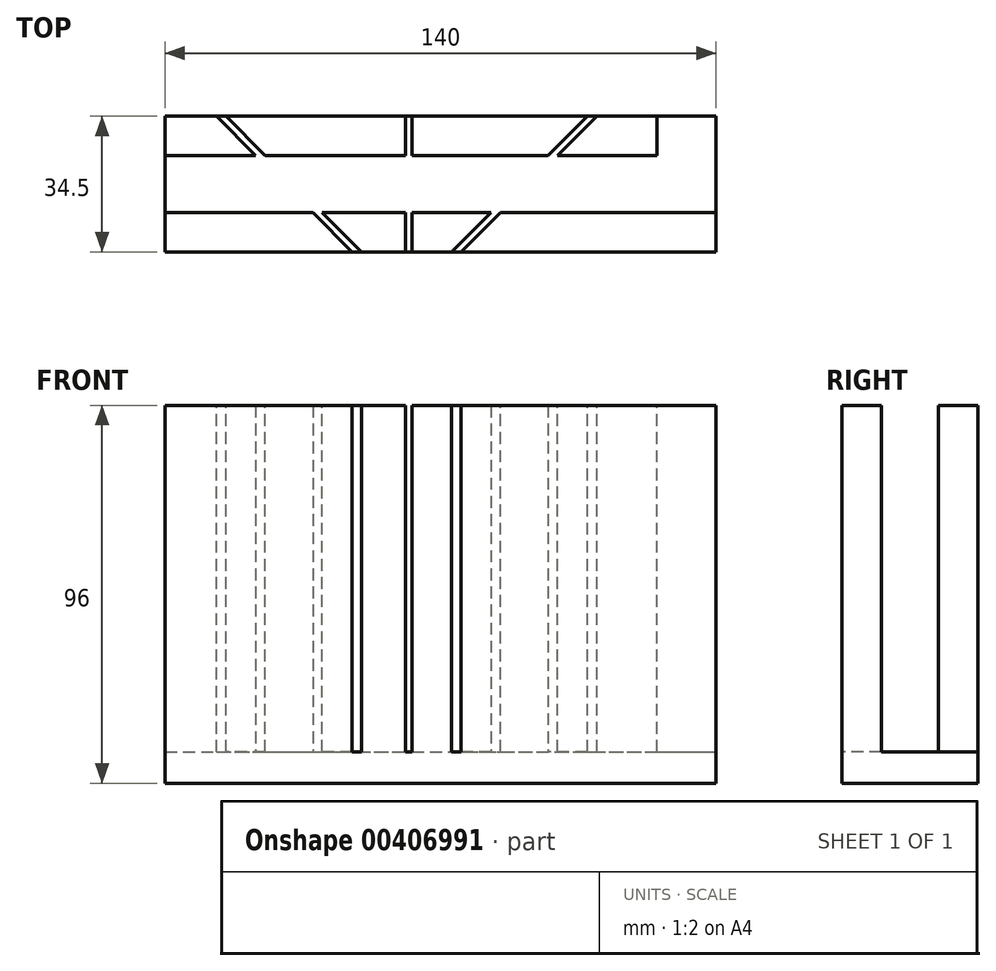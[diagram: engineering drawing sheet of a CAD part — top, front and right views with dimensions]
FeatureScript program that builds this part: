
annotation { "Feature Type Name" : "Feature", "Feature Type Description" : "" }
export const myFeature = defineFeature(function(context is Context, id is Id, definition is map)
    precondition{}
    {
        {
            var Q0;
            Q0=qCreatedBy(makeId("Top.planeOp"),FACE);
            var sketch = newSketch(context, id + "F0", { "sketchPlane" : qUnion([Q0])});
            skLineSegment(sketch, "E0.bottom", {"start": v(-28.5, 12) * mm, "end": v(111.5, 12) * mm});
            skLineSegment(sketch, "E0.top", {"start": v(-28.5, -22.5) * mm, "end": v(111.5, -22.5) * mm});
            skLineSegment(sketch, "E0.left", {"start": v(-28.5, 12) * mm, "end": v(-28.5, -22.5) * mm});
            skLineSegment(sketch, "E0.right", {"start": v(111.5, 12) * mm, "end": v(111.5, -22.5) * mm});
            skSolve(sketch);
        }
        {
            var Q0;
            Q0 = qSketchRegion(id + "F0", true);
            extrude(context, id + "F1", {"entities" : qUnion([Q0]), "depth" : 96 * mm});
        }
        {
            var Q0;
            Q0=makeQuery(id+"F1.opExtrude","CAP_FACE",FACE,{"disambiguationData":[OSD([sQuery(id+"F0.wireOp",EDGE,"E0.bottom"),sQuery(id+"F0.wireOp",EDGE,"E0.top"),sQuery(id+"F0.wireOp",EDGE,"E0.left"),sQuery(id+"F0.wireOp",EDGE,"E0.right")])],"isStart":false});
            var sketch = newSketch(context, id + "F2", { "sketchPlane" : qUnion([Q0])});
            skLineSegment(sketch, "E1.bottom", {"start": v(-28.5, 2) * mm, "end": v(111.5, 2) * mm});
            skLineSegment(sketch, "E1.top", {"start": v(-28.5, -12.5) * mm, "end": v(111.5, -12.5) * mm});
            skLineSegment(sketch, "E1.left", {"start": v(-28.5, 2) * mm, "end": v(-28.5, -12.5) * mm});
            skLineSegment(sketch, "E1.right", {"start": v(111.5, 2) * mm, "end": v(111.5, -12.5) * mm});
            skLineSegment(sketch, "E2.bottom", {"start": v(111.5, -5.25) * mm, "end": v(-28.5, -5.25) * mm, "construction": true});
            skLineSegment(sketch, "E2.top", {"start": v(111.5, -5.25) * mm, "end": v(-28.5, -5.25) * mm, "construction": true});
            skLineSegment(sketch, "E2.left", {"start": v(111.5, -5.25) * mm, "end": v(111.5, -5.25) * mm});
            skLineSegment(sketch, "E2.right", {"start": v(-28.5, -5.25) * mm, "end": v(-28.5, -5.25) * mm});
            skSolve(sketch);
        }
        {
            var Q0;
            Q0 = qSketchRegion(id + "F2", true);
            extrude(context, id + "F3", {"entities" : qUnion([Q0]), "operationType" : NewBodyOperationType.REMOVE, "oppositeDirection" : true, "depth" : 88 * mm});
        }
        {
            var Q0;
            {var subQ0=sQuery(id+"F0.wireOp",EDGE,"E0.bottom");var subQ1=sQuery(id+"F0.wireOp",EDGE,"E0.right");var subQ2=sQuery(id+"F0.wireOp",EDGE,"E0.left");Q0=makeQuery(id+"F3.boolean.opBoolean","SPLIT",FACE,{"disambiguationData":[TD([makeQuery(id+"F1.opExtrude","SWEPT_FACE",FACE,{"disambiguationData":[OSD([subQ0])]})])],"derivedFrom":makeQuery(id+"F1.opExtrude","CAP_FACE",FACE,{"disambiguationData":[OSD([subQ0,sQuery(id+"F0.wireOp",EDGE,"E0.top"),subQ2,subQ1])],"isStart":false})});}
            var sketch = newSketch(context, id + "F4", { "sketchPlane" : qUnion([Q0])});
            skLineSegment(sketch, "E3", {"start": v(-15.47, 12) * mm, "end": v(20.02, -23.5) * mm});
            skLineSegment(sketch, "E4", {"start": v(20.02, -23.5) * mm, "end": v(22.43, -23.5) * mm});
            skLineSegment(sketch, "E5", {"start": v(22.43, -23.5) * mm, "end": v(-13.07, 12) * mm});
            skLineSegment(sketch, "E6", {"start": v(-13.07, 12) * mm, "end": v(-15.47, 12) * mm});
            skLineSegment(sketch, "E7", {"start": v(78.76, 12) * mm, "end": v(42.6, -24.16) * mm});
            skLineSegment(sketch, "E8", {"start": v(42.6, -24.16) * mm, "end": v(45, -24.16) * mm});
            skLineSegment(sketch, "E9", {"start": v(45, -24.16) * mm, "end": v(81.16, 12) * mm});
            skLineSegment(sketch, "E10", {"start": v(81.16, 12) * mm, "end": v(78.76, 12) * mm});
            skLineSegment(sketch, "E11.bottom", {"start": v(32.51, 12) * mm, "end": v(34.21, 12) * mm});
            skLineSegment(sketch, "E11.top", {"start": v(32.51, -23.5) * mm, "end": v(34.21, -23.5) * mm});
            skLineSegment(sketch, "E11.left", {"start": v(32.51, 12) * mm, "end": v(32.51, -23.5) * mm});
            skLineSegment(sketch, "E11.right", {"start": v(34.21, 12) * mm, "end": v(34.21, -23.5) * mm});
            skLineSegment(sketch, "E12.bottom", {"start": v(111.5, 12) * mm, "end": v(96.46, 12) * mm});
            skLineSegment(sketch, "E12.top", {"start": v(111.5, 2) * mm, "end": v(96.46, 2) * mm});
            skLineSegment(sketch, "E12.left", {"start": v(111.5, 12) * mm, "end": v(111.5, 2) * mm});
            skLineSegment(sketch, "E12.right", {"start": v(96.46, 12) * mm, "end": v(96.46, 2) * mm});
            skSolve(sketch);
        }
        {
            var Q0;
            Q0 = qSketchRegion(id + "F4", true);
            extrude(context, id + "F5", {"entities" : qUnion([Q0]), "operationType" : NewBodyOperationType.REMOVE, "oppositeDirection" : true, "depth" : 88 * mm});
        }
    });
